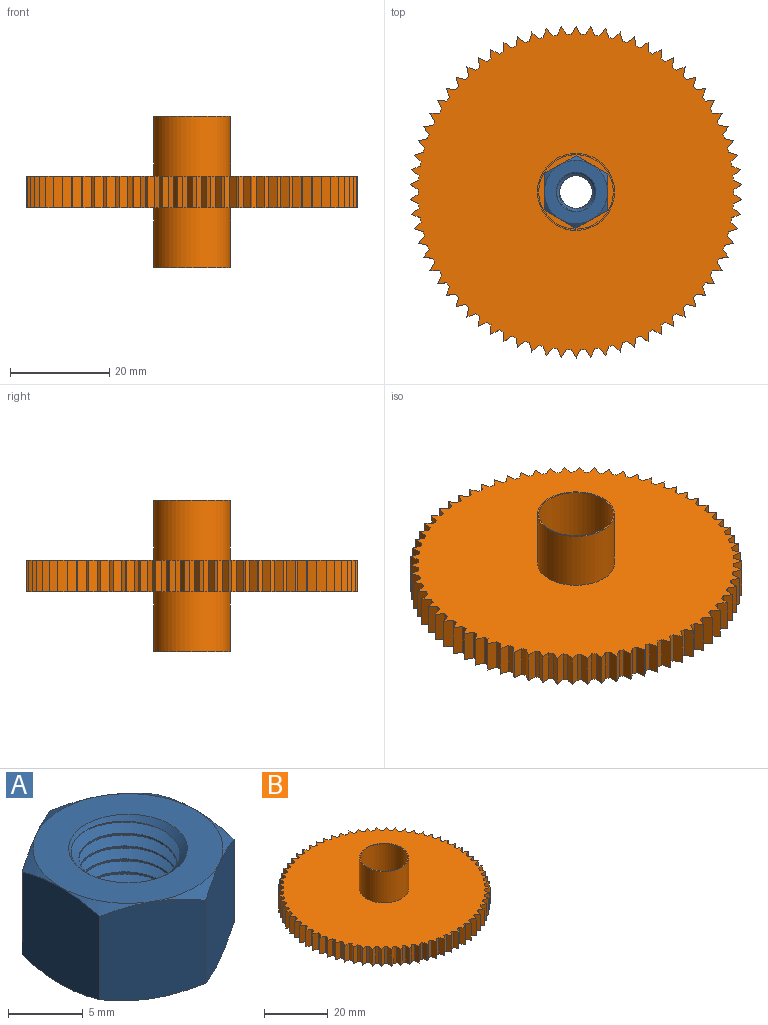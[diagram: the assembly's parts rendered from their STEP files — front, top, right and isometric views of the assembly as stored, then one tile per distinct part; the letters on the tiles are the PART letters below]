
ASSEMBLY  parts=2 mates=1
PART A: 26 faces, bbox 15.3x15.3x9.5 mm
  f0: plane 12.7x12.7mm, normal (0,0,1), area 77.2mm2, adj f7,f12,f13,f14,f15,f16,f17,f18
  f1: plane 8.55x6.95mm, normal (-0.5,0.87,0), area 55.3mm2, adj f2,f6,f13,f18,f21,f22
  f2: plane 8.55x7.94mm, normal (-1,0,0), area 55.3mm2, adj f1,f3,f17,f18,f22,f23
  f3: plane 8.55x6.95mm, normal (-0.5,-0.87,0), area 55.3mm2, adj f2,f4,f16,f17,f23,f24
  f4: plane 8.55x6.95mm, normal (0.5,-0.87,0), area 55.3mm2, adj f3,f5,f15,f16,f24,f25
  f5: plane 8.55x7.94mm, normal (1,0,0), area 55.3mm2, adj f4,f6,f14,f15,f20,f25
  f6: plane 8.55x6.95mm, normal (0.5,0.87,0), area 55.3mm2, adj f1,f5,f13,f14,f20,f21
  f7: cylinder r=3.97mm len=7.94mm, axis (0,0,-1), area 24.7mm2, adj f0,f8,f9,f11
  f8: plane 12.7x12.7mm, normal (0,0,-1), area 77.2mm2, adj f7,f19,f20,f21,f22,f23,f24,f25
  f9: bspline ~8.6x7.94mm, area 124.2mm2, adj f7,f10,f12,f19
  f10: cylinder r=3.28mm len=6.56mm, axis (0,0,1), area 16.9mm2, adj f9,f11,f12,f19
  f11: bspline ~8.33x7.94mm, area 124.1mm2, adj f7,f10,f12,f19
  f12: cone r=3.7mm half-angle=45deg, axis (0,0,1), area 11.3mm2, adj f0,f9,f10,f11
  f13: cone r=6.35mm half-angle=60deg, axis (0,0,-1), area 4mm2, adj f0,f1,f6
  f14: cone r=6.35mm half-angle=60deg, axis (0,0,-1), area 4mm2, adj f0,f5,f6
  f15: cone r=6.35mm half-angle=60deg, axis (0,0,-1), area 4mm2, adj f0,f4,f5
  f16: cone r=6.35mm half-angle=60deg, axis (0,0,-1), area 4mm2, adj f0,f3,f4
  f17: cone r=6.35mm half-angle=60deg, axis (0,0,-1), area 4mm2, adj f0,f2,f3
  f18: cone r=6.35mm half-angle=60deg, axis (0,0,-1), area 4mm2, adj f0,f1,f2
  f19: cone r=3.7mm half-angle=45deg, axis (0,0,-1), area 11.3mm2, adj f8,f9,f10,f11
  f20: cone r=6.35mm half-angle=60deg, axis (0,0,1), area 4mm2, adj f5,f6,f8
  f21: cone r=6.35mm half-angle=60deg, axis (0,0,1), area 4mm2, adj f1,f6,f8
  f22: cone r=6.35mm half-angle=60deg, axis (0,0,1), area 4mm2, adj f1,f2,f8
  f23: cone r=6.35mm half-angle=60deg, axis (0,0,1), area 4mm2, adj f2,f3,f8
  f24: cone r=6.35mm half-angle=60deg, axis (0,0,1), area 4mm2, adj f3,f4,f8
  f25: cone r=6.35mm half-angle=60deg, axis (0,0,1), area 4mm2, adj f4,f5,f8
PART B: 226 faces, bbox 66.7x66.8x30.5 mm
  f0: plane 14.99x14.99mm, normal (0,0,1), area 36.7mm2, adj f2,f3,f4,f5,f6,f7,f223
  f1: plane 14.99x14.99mm, normal (0,0,-1), area 36.7mm2, adj f2,f3,f4,f5,f6,f7,f8
  f2: plane 6.37x6.35mm, normal (-0.49,0.87,0), area 46.6mm2, adj f0,f1,f3,f7
  f3: plane 6.35x6.33mm, normal (0.51,0.86,0), area 46.6mm2, adj f0,f1,f2,f4
  f4: plane 7.33x6.35mm, normal (1,-0.01,0), area 46.6mm2, adj f0,f1,f3,f5
  f5: plane 6.37x6.35mm, normal (0.49,-0.87,0), area 46.6mm2, adj f0,f1,f4,f6
  f6: plane 6.35x6.33mm, normal (-0.51,-0.86,0), area 46.6mm2, adj f0,f1,f5,f7
  f7: plane 7.33x6.35mm, normal (-1,0.01,0), area 46.6mm2, adj f0,f1,f2,f6
  f8: cylinder r=7.49mm len=14.99mm, axis (0,0,-1), area 568mm2, adj f1,f9
  f9: plane 15.49x15.49mm, normal (0,0,-1), area 12.2mm2, adj f8,f10
  f10: cylinder r=7.75mm len=15.49mm, axis (0,0,-1), area 587.3mm2, adj f9,f222
  f11: plane 6.35x1.45mm, normal (0.76,0.65,0), area 12.1mm2, adj f12,f220,f221,f222
  f12: plane 6.35x1.79mm, normal (-0.94,0.34,0), area 12.1mm2, adj f11,f13,f220,f222
  f13: cylinder r=31.75mm len=6.35mm, axis (0,0,-1), area 6mm2, adj f12,f14,f220,f222
  f14: plane 6.35x1.36mm, normal (0.7,0.71,0), area 12.1mm2, adj f13,f15,f220,f222
  f15: plane 6.35x1.84mm, normal (-0.97,0.25,0), area 12.1mm2, adj f14,f16,f220,f222
  f16: cylinder r=31.75mm len=6.35mm, axis (0,0,-1), area 6mm2, adj f15,f17,f220,f222
  f17: plane 6.35x1.47mm, normal (0.64,0.77,0), area 12.1mm2, adj f16,f18,f220,f222
  f18: plane 6.35x1.88mm, normal (-0.99,0.16,0), area 12.1mm2, adj f17,f19,f220,f222
  f19: cylinder r=31.75mm len=6.35mm, axis (0,0,-1), area 6mm2, adj f18,f20,f220,f222
  f20: plane 6.35x1.57mm, normal (0.56,0.83,0), area 12.1mm2, adj f19,f21,f220,f222
  f21: plane 6.35x1.9mm, normal (-1,0.07,0), area 12.1mm2, adj f20,f22,f220,f222
  f22: cylinder r=31.75mm len=6.35mm, axis (0,0,-1), area 6mm2, adj f21,f23,f220,f222
  f23: plane 6.35x1.66mm, normal (0.49,0.87,0), area 12.1mm2, adj f22,f24,f220,f222
  f24: plane 6.35x1.9mm, normal (-1,-0.01,0), area 12.1mm2, adj f23,f25,f220,f222
  f25: cylinder r=31.75mm len=6.35mm, axis (0,0,-1), area 6mm2, adj f24,f26,f220,f222
  f26: plane 6.35x1.74mm, normal (0.41,0.91,0), area 12.1mm2, adj f25,f27,f220,f222
  f27: plane 6.35x1.89mm, normal (-0.99,-0.1,0), area 12.1mm2, adj f26,f28,f220,f222
  f28: cylinder r=31.75mm len=6.35mm, axis (0,0,-1), area 6mm2, adj f27,f29,f220,f222
  f29: plane 6.35x1.8mm, normal (0.32,0.95,0), area 12.1mm2, adj f28,f30,f220,f222
  f30: plane 6.35x1.87mm, normal (-0.98,-0.19,0), area 12.1mm2, adj f29,f31,f220,f222
  f31: cylinder r=31.75mm len=6.35mm, axis (0,0,-1), area 6mm2, adj f30,f32,f220,f222
  f32: plane 6.35x1.85mm, normal (0.24,0.97,0), area 12.1mm2, adj f31,f33,f220,f222
  f33: plane 6.35x1.83mm, normal (-0.96,-0.28,0), area 12.1mm2, adj f32,f34,f220,f222
  f34: cylinder r=31.75mm len=6.35mm, axis (0,0,-1), area 6mm2, adj f33,f35,f220,f222
  f35: plane 6.35x1.88mm, normal (0.15,0.99,0), area 12.1mm2, adj f34,f36,f220,f222
  f36: plane 6.35x1.77mm, normal (-0.93,-0.37,0), area 12.1mm2, adj f35,f37,f220,f222
  f37: cylinder r=31.75mm len=6.35mm, axis (0,0,-1), area 6mm2, adj f36,f38,f220,f222
  f38: plane 6.35x1.9mm, normal (0.06,1,0), area 12.1mm2, adj f37,f39,f220,f222
  f39: plane 6.35x1.7mm, normal (-0.89,-0.45,0), area 12.1mm2, adj f38,f40,f220,f222
  f40: cylinder r=31.75mm len=6.35mm, axis (0,0,-1), area 6mm2, adj f39,f41,f220,f222
  f41: plane 6.35x1.9mm, normal (-0.03,1,0), area 12.1mm2, adj f40,f42,f220,f222
  f42: plane 6.35x1.62mm, normal (-0.85,-0.53,0), area 12.1mm2, adj f41,f43,f220,f222
  f43: cylinder r=31.75mm len=6.35mm, axis (0,0,-1), area 6mm2, adj f42,f44,f220,f222
  f44: plane 6.35x1.89mm, normal (-0.12,0.99,0), area 12.1mm2, adj f43,f45,f220,f222
  f45: plane 6.35x1.52mm, normal (-0.8,-0.6,0), area 12.1mm2, adj f44,f46,f220,f222
  f46: cylinder r=31.75mm len=6.35mm, axis (0,0,-1), area 6mm2, adj f45,f47,f220,f222
  f47: plane 6.35x1.86mm, normal (-0.21,0.98,0), area 12.1mm2, adj f46,f48,f220,f222
  f48: plane 6.35x1.42mm, normal (-0.74,-0.67,0), area 12.1mm2, adj f47,f49,f220,f222
  f49: cylinder r=31.75mm len=6.35mm, axis (0,0,-1), area 6mm2, adj f48,f50,f220,f222
  f50: plane 6.35x1.82mm, normal (-0.29,0.96,0), area 12.1mm2, adj f49,f51,f220,f222
  f51: plane 6.35x1.4mm, normal (-0.68,-0.73,0), area 12.1mm2, adj f50,f52,f220,f222
  f52: cylinder r=31.75mm len=6.35mm, axis (0,0,-1), area 6mm2, adj f51,f53,f220,f222
  f53: plane 6.35x1.76mm, normal (-0.38,0.93,0), area 12.1mm2, adj f52,f54,f220,f222
  f54: plane 6.35x1.51mm, normal (-0.61,-0.79,0), area 12.1mm2, adj f53,f55,f220,f222
  f55: cylinder r=31.75mm len=6.35mm, axis (0,0,-1), area 6mm2, adj f54,f56,f220,f222
  f56: plane 6.35x1.69mm, normal (-0.46,0.89,0), area 12.1mm2, adj f55,f57,f220,f222
  f57: plane 6.35x1.61mm, normal (-0.54,-0.84,0), area 12.1mm2, adj f56,f58,f220,f222
  f58: cylinder r=31.75mm len=6.35mm, axis (0,0,-1), area 6mm2, adj f57,f59,f220,f222
  f59: plane 6.35x1.61mm, normal (-0.54,0.84,0), area 12.1mm2, adj f58,f60,f220,f222
  f60: plane 6.35x1.69mm, normal (-0.46,-0.89,0), area 12.1mm2, adj f59,f61,f220,f222
  f61: cylinder r=31.75mm len=6.35mm, axis (0,0,-1), area 6mm2, adj f60,f62,f220,f222
  f62: plane 6.35x1.51mm, normal (-0.61,0.79,0), area 12.1mm2, adj f61,f63,f220,f222
  f63: plane 6.35x1.76mm, normal (-0.38,-0.93,0), area 12.1mm2, adj f62,f64,f220,f222
  f64: cylinder r=31.75mm len=6.35mm, axis (0,0,-1), area 6mm2, adj f63,f65,f220,f222
  f65: plane 6.35x1.4mm, normal (-0.68,0.73,0), area 12.1mm2, adj f64,f66,f220,f222
  f66: plane 6.35x1.82mm, normal (-0.29,-0.96,0), area 12.1mm2, adj f65,f67,f220,f222
  f67: cylinder r=31.75mm len=6.35mm, axis (0,0,-1), area 6mm2, adj f66,f68,f220,f222
  f68: plane 6.35x1.42mm, normal (-0.74,0.67,0), area 12.1mm2, adj f67,f69,f220,f222
  f69: plane 6.35x1.86mm, normal (-0.21,-0.98,0), area 12.1mm2, adj f68,f70,f220,f222
  f70: cylinder r=31.75mm len=6.35mm, axis (0,0,-1), area 6mm2, adj f69,f71,f220,f222
  f71: plane 6.35x1.52mm, normal (-0.8,0.6,0), area 12.1mm2, adj f70,f72,f220,f222
  f72: plane 6.35x1.89mm, normal (-0.12,-0.99,0), area 12.1mm2, adj f71,f73,f220,f222
  f73: cylinder r=31.75mm len=6.35mm, axis (0,0,-1), area 6mm2, adj f72,f74,f220,f222
  f74: plane 6.35x1.62mm, normal (-0.85,0.53,0), area 12.1mm2, adj f73,f75,f220,f222
  f75: plane 6.35x1.9mm, normal (-0.03,-1,0), area 12.1mm2, adj f74,f76,f220,f222
  f76: cylinder r=31.75mm len=6.35mm, axis (0,0,-1), area 6mm2, adj f75,f77,f220,f222
  f77: plane 6.35x1.7mm, normal (-0.89,0.45,0), area 12.1mm2, adj f76,f78,f220,f222
  f78: plane 6.35x1.9mm, normal (0.06,-1,0), area 12.1mm2, adj f77,f79,f220,f222
  f79: cylinder r=31.75mm len=6.35mm, axis (0,0,-1), area 6mm2, adj f78,f80,f220,f222
  f80: plane 6.35x1.77mm, normal (-0.93,0.37,0), area 12.1mm2, adj f79,f81,f220,f222
  f81: plane 6.35x1.88mm, normal (0.15,-0.99,0), area 12.1mm2, adj f80,f82,f220,f222
  f82: cylinder r=31.75mm len=6.35mm, axis (0,0,-1), area 6mm2, adj f81,f83,f220,f222
  f83: plane 6.35x1.83mm, normal (-0.96,0.28,0), area 12.1mm2, adj f82,f84,f220,f222
  f84: plane 6.35x1.85mm, normal (0.24,-0.97,0), area 12.1mm2, adj f83,f85,f220,f222
  f85: cylinder r=31.75mm len=6.35mm, axis (0,0,-1), area 6mm2, adj f84,f86,f220,f222
  f86: plane 6.35x1.87mm, normal (-0.98,0.19,0), area 12.1mm2, adj f85,f87,f220,f222
  f87: plane 6.35x1.8mm, normal (0.32,-0.95,0), area 12.1mm2, adj f86,f88,f220,f222
  f88: cylinder r=31.75mm len=6.35mm, axis (0,0,-1), area 6mm2, adj f87,f89,f220,f222
  f89: plane 6.35x1.89mm, normal (-0.99,0.1,0), area 12.1mm2, adj f88,f90,f220,f222
  f90: plane 6.35x1.74mm, normal (0.41,-0.91,0), area 12.1mm2, adj f89,f91,f220,f222
  f91: cylinder r=31.75mm len=6.35mm, axis (0,0,-1), area 6mm2, adj f90,f92,f220,f222
  f92: plane 6.35x1.9mm, normal (-1,0.01,0), area 12.1mm2, adj f91,f93,f220,f222
  f93: plane 6.35x1.66mm, normal (0.49,-0.87,0), area 12.1mm2, adj f92,f94,f220,f222
  f94: cylinder r=31.75mm len=6.35mm, axis (0,0,-1), area 6mm2, adj f93,f95,f220,f222
  f95: plane 6.35x1.9mm, normal (-1,-0.07,0), area 12.1mm2, adj f94,f96,f220,f222
  f96: plane 6.35x1.57mm, normal (0.56,-0.83,0), area 12.1mm2, adj f95,f97,f220,f222
  f97: cylinder r=31.75mm len=6.35mm, axis (0,0,-1), area 6mm2, adj f96,f98,f220,f222
  f98: plane 6.35x1.88mm, normal (-0.99,-0.16,0), area 12.1mm2, adj f97,f99,f220,f222
  f99: plane 6.35x1.47mm, normal (0.64,-0.77,0), area 12.1mm2, adj f98,f100,f220,f222
  f100: cylinder r=31.75mm len=6.35mm, axis (0,0,-1), area 6mm2, adj f99,f101,f220,f222
  f101: plane 6.35x1.84mm, normal (-0.97,-0.25,0), area 12.1mm2, adj f100,f102,f220,f222
  f102: plane 6.35x1.36mm, normal (0.7,-0.71,0), area 12.1mm2, adj f101,f103,f220,f222
  f103: cylinder r=31.75mm len=6.35mm, axis (0,0,-1), area 6mm2, adj f102,f104,f220,f222
  f104: plane 6.35x1.79mm, normal (-0.94,-0.34,0), area 12.1mm2, adj f103,f105,f220,f222
  f105: plane 6.35x1.45mm, normal (0.76,-0.65,0), area 12.1mm2, adj f104,f106,f220,f222
  f106: cylinder r=31.75mm len=6.35mm, axis (0,0,-1), area 6mm2, adj f105,f107,f220,f222
  f107: plane 6.35x1.73mm, normal (-0.91,-0.42,0), area 12.1mm2, adj f106,f108,f220,f222
  f108: plane 6.35x1.56mm, normal (0.82,-0.58,0), area 12.1mm2, adj f107,f109,f220,f222
  f109: cylinder r=31.75mm len=6.35mm, axis (0,0,-1), area 6mm2, adj f108,f110,f220,f222
  f110: plane 6.35x1.65mm, normal (-0.87,-0.5,0), area 12.1mm2, adj f109,f111,f220,f222
  f111: plane 6.35x1.65mm, normal (0.87,-0.5,0), area 12.1mm2, adj f110,f112,f220,f222
  f112: cylinder r=31.75mm len=6.35mm, axis (0,0,-1), area 6mm2, adj f111,f113,f220,f222
  f113: plane 6.35x1.56mm, normal (-0.82,-0.58,0), area 12.1mm2, adj f112,f114,f220,f222
  f114: plane 6.35x1.73mm, normal (0.91,-0.42,0), area 12.1mm2, adj f113,f115,f220,f222
  f115: cylinder r=31.75mm len=6.35mm, axis (0,0,-1), area 6mm2, adj f114,f116,f220,f222
  f116: plane 6.35x1.45mm, normal (-0.76,-0.65,0), area 12.1mm2, adj f115,f117,f220,f222
  f117: plane 6.35x1.79mm, normal (0.94,-0.34,0), area 12.1mm2, adj f116,f118,f220,f222
  f118: cylinder r=31.75mm len=6.35mm, axis (0,0,-1), area 6mm2, adj f117,f119,f220,f222
  f119: plane 6.35x1.36mm, normal (-0.7,-0.71,0), area 12.1mm2, adj f118,f120,f220,f222
  f120: plane 6.35x1.84mm, normal (0.97,-0.25,0), area 12.1mm2, adj f119,f121,f220,f222
  f121: cylinder r=31.75mm len=6.35mm, axis (0,0,-1), area 6mm2, adj f120,f122,f220,f222
  f122: plane 6.35x1.47mm, normal (-0.64,-0.77,0), area 12.1mm2, adj f121,f123,f220,f222
  f123: plane 6.35x1.88mm, normal (0.99,-0.16,0), area 12.1mm2, adj f122,f124,f220,f222
  f124: cylinder r=31.75mm len=6.35mm, axis (0,0,-1), area 6mm2, adj f123,f125,f220,f222
  f125: plane 6.35x1.57mm, normal (-0.56,-0.83,0), area 12.1mm2, adj f124,f126,f220,f222
  f126: plane 6.35x1.9mm, normal (1,-0.07,0), area 12.1mm2, adj f125,f127,f220,f222
  f127: cylinder r=31.75mm len=6.35mm, axis (0,0,-1), area 6mm2, adj f126,f128,f220,f222
  f128: plane 6.35x1.66mm, normal (-0.49,-0.87,0), area 12.1mm2, adj f127,f129,f220,f222
  f129: plane 6.35x1.9mm, normal (1,0.01,0), area 12.1mm2, adj f128,f130,f220,f222
  f130: cylinder r=31.75mm len=6.35mm, axis (0,0,-1), area 6mm2, adj f129,f131,f220,f222
  f131: plane 6.35x1.74mm, normal (-0.41,-0.91,0), area 12.1mm2, adj f130,f132,f220,f222
  f132: plane 6.35x1.89mm, normal (0.99,0.1,0), area 12.1mm2, adj f131,f133,f220,f222
  f133: cylinder r=31.75mm len=6.35mm, axis (0,0,-1), area 6mm2, adj f132,f134,f220,f222
  f134: plane 6.35x1.8mm, normal (-0.32,-0.95,0), area 12.1mm2, adj f133,f135,f220,f222
  f135: plane 6.35x1.87mm, normal (0.98,0.19,0), area 12.1mm2, adj f134,f136,f220,f222
  f136: cylinder r=31.75mm len=6.35mm, axis (0,0,-1), area 6mm2, adj f135,f137,f220,f222
  f137: plane 6.35x1.85mm, normal (-0.24,-0.97,0), area 12.1mm2, adj f136,f138,f220,f222
  f138: plane 6.35x1.83mm, normal (0.96,0.28,0), area 12.1mm2, adj f137,f139,f220,f222
  f139: cylinder r=31.75mm len=6.35mm, axis (0,0,-1), area 6mm2, adj f138,f140,f220,f222
  f140: plane 6.35x1.88mm, normal (-0.15,-0.99,0), area 12.1mm2, adj f139,f141,f220,f222
  f141: plane 6.35x1.77mm, normal (0.93,0.37,0), area 12.1mm2, adj f140,f142,f220,f222
  f142: cylinder r=31.75mm len=6.35mm, axis (0,0,-1), area 6mm2, adj f141,f143,f220,f222
  f143: plane 6.35x1.9mm, normal (-0.06,-1,0), area 12.1mm2, adj f142,f144,f220,f222
  f144: plane 6.35x1.7mm, normal (0.89,0.45,0), area 12.1mm2, adj f143,f145,f220,f222
  f145: cylinder r=31.75mm len=6.35mm, axis (0,0,-1), area 6mm2, adj f144,f146,f220,f222
  f146: plane 6.35x1.9mm, normal (0.03,-1,0), area 12.1mm2, adj f145,f147,f220,f222
  f147: plane 6.35x1.62mm, normal (0.85,0.53,0), area 12.1mm2, adj f146,f148,f220,f222
  f148: cylinder r=31.75mm len=6.35mm, axis (0,0,-1), area 6mm2, adj f147,f149,f220,f222
  f149: plane 6.35x1.89mm, normal (0.12,-0.99,0), area 12.1mm2, adj f148,f150,f220,f222
  f150: plane 6.35x1.52mm, normal (0.8,0.6,0), area 12.1mm2, adj f149,f151,f220,f222
  f151: cylinder r=31.75mm len=6.35mm, axis (0,0,-1), area 6mm2, adj f150,f152,f220,f222
  f152: plane 6.35x1.86mm, normal (0.21,-0.98,0), area 12.1mm2, adj f151,f153,f220,f222
  f153: plane 6.35x1.42mm, normal (0.74,0.67,0), area 12.1mm2, adj f152,f154,f220,f222
  f154: cylinder r=31.75mm len=6.35mm, axis (0,0,-1), area 6mm2, adj f153,f155,f220,f222
  f155: plane 6.35x1.82mm, normal (0.29,-0.96,0), area 12.1mm2, adj f154,f156,f220,f222
  f156: plane 6.35x1.4mm, normal (0.68,0.73,0), area 12.1mm2, adj f155,f157,f220,f222
  f157: cylinder r=31.75mm len=6.35mm, axis (0,0,-1), area 6mm2, adj f156,f158,f220,f222
  f158: plane 6.35x1.76mm, normal (0.38,-0.93,0), area 12.1mm2, adj f157,f159,f220,f222
  f159: plane 6.35x1.51mm, normal (0.61,0.79,0), area 12.1mm2, adj f158,f160,f220,f222
  f160: cylinder r=31.75mm len=6.35mm, axis (0,0,-1), area 6mm2, adj f159,f161,f220,f222
  f161: plane 6.35x1.69mm, normal (0.46,-0.89,0), area 12.1mm2, adj f160,f162,f220,f222
  f162: plane 6.35x1.61mm, normal (0.54,0.84,0), area 12.1mm2, adj f161,f163,f220,f222
  f163: cylinder r=31.75mm len=6.35mm, axis (0,0,-1), area 6mm2, adj f162,f164,f220,f222
  f164: plane 6.35x1.61mm, normal (0.54,-0.84,0), area 12.1mm2, adj f163,f165,f220,f222
  f165: plane 6.35x1.69mm, normal (0.46,0.89,0), area 12.1mm2, adj f164,f166,f220,f222
  f166: cylinder r=31.75mm len=6.35mm, axis (0,0,-1), area 6mm2, adj f165,f167,f220,f222
  f167: plane 6.35x1.51mm, normal (0.61,-0.79,0), area 12.1mm2, adj f166,f168,f220,f222
  f168: plane 6.35x1.76mm, normal (0.38,0.93,0), area 12.1mm2, adj f167,f169,f220,f222
  f169: cylinder r=31.75mm len=6.35mm, axis (0,0,-1), area 6mm2, adj f168,f170,f220,f222
  f170: plane 6.35x1.4mm, normal (0.68,-0.73,0), area 12.1mm2, adj f169,f171,f220,f222
  f171: plane 6.35x1.82mm, normal (0.29,0.96,0), area 12.1mm2, adj f170,f172,f220,f222
  f172: cylinder r=31.75mm len=6.35mm, axis (0,0,-1), area 6mm2, adj f171,f173,f220,f222
  f173: plane 6.35x1.42mm, normal (0.74,-0.67,0), area 12.1mm2, adj f172,f174,f220,f222
  f174: plane 6.35x1.86mm, normal (0.21,0.98,0), area 12.1mm2, adj f173,f175,f220,f222
  f175: cylinder r=31.75mm len=6.35mm, axis (0,0,-1), area 6mm2, adj f174,f176,f220,f222
  f176: plane 6.35x1.52mm, normal (0.8,-0.6,0), area 12.1mm2, adj f175,f177,f220,f222
  f177: plane 6.35x1.89mm, normal (0.12,0.99,0), area 12.1mm2, adj f176,f178,f220,f222
  f178: cylinder r=31.75mm len=6.35mm, axis (0,0,-1), area 6mm2, adj f177,f179,f220,f222
  f179: plane 6.35x1.62mm, normal (0.85,-0.53,0), area 12.1mm2, adj f178,f180,f220,f222
  f180: plane 6.35x1.9mm, normal (0.03,1,0), area 12.1mm2, adj f179,f181,f220,f222
  f181: cylinder r=31.75mm len=6.35mm, axis (0,0,-1), area 6mm2, adj f180,f182,f220,f222
  f182: plane 6.35x1.7mm, normal (0.89,-0.45,0), area 12.1mm2, adj f181,f183,f220,f222
  f183: plane 6.35x1.9mm, normal (-0.06,1,0), area 12.1mm2, adj f182,f184,f220,f222
  f184: cylinder r=31.75mm len=6.35mm, axis (0,0,-1), area 6mm2, adj f183,f185,f220,f222
  f185: plane 6.35x1.77mm, normal (0.93,-0.37,0), area 12.1mm2, adj f184,f186,f220,f222
  f186: plane 6.35x1.88mm, normal (-0.15,0.99,0), area 12.1mm2, adj f185,f187,f220,f222
  f187: cylinder r=31.75mm len=6.35mm, axis (0,0,-1), area 6mm2, adj f186,f188,f220,f222
  f188: plane 6.35x1.83mm, normal (0.96,-0.28,0), area 12.1mm2, adj f187,f189,f220,f222
  f189: plane 6.35x1.85mm, normal (-0.24,0.97,0), area 12.1mm2, adj f188,f190,f220,f222
  f190: cylinder r=31.75mm len=6.35mm, axis (0,0,-1), area 6mm2, adj f189,f191,f220,f222
  f191: plane 6.35x1.87mm, normal (0.98,-0.19,0), area 12.1mm2, adj f190,f192,f220,f222
  f192: plane 6.35x1.8mm, normal (-0.32,0.95,0), area 12.1mm2, adj f191,f193,f220,f222
  f193: cylinder r=31.75mm len=6.35mm, axis (0,0,-1), area 6mm2, adj f192,f194,f220,f222
  f194: plane 6.35x1.89mm, normal (0.99,-0.1,0), area 12.1mm2, adj f193,f195,f220,f222
  f195: plane 6.35x1.74mm, normal (-0.41,0.91,0), area 12.1mm2, adj f194,f196,f220,f222
  f196: cylinder r=31.75mm len=6.35mm, axis (0,0,-1), area 6mm2, adj f195,f197,f220,f222
  f197: plane 6.35x1.9mm, normal (1,-0.01,0), area 12.1mm2, adj f196,f198,f220,f222
  f198: plane 6.35x1.66mm, normal (-0.49,0.87,0), area 12.1mm2, adj f197,f199,f220,f222
  f199: cylinder r=31.75mm len=6.35mm, axis (0,0,-1), area 6mm2, adj f198,f200,f220,f222
  f200: plane 6.35x1.9mm, normal (1,0.07,0), area 12.1mm2, adj f199,f201,f220,f222
  f201: plane 6.35x1.57mm, normal (-0.56,0.83,0), area 12.1mm2, adj f200,f202,f220,f222
  f202: cylinder r=31.75mm len=6.35mm, axis (0,0,-1), area 6mm2, adj f201,f203,f220,f222
  f203: plane 6.35x1.88mm, normal (0.99,0.16,0), area 12.1mm2, adj f202,f204,f220,f222
  f204: plane 6.35x1.47mm, normal (-0.64,0.77,0), area 12.1mm2, adj f203,f205,f220,f222
  f205: cylinder r=31.75mm len=6.35mm, axis (0,0,-1), area 6mm2, adj f204,f206,f220,f222
  f206: plane 6.35x1.84mm, normal (0.97,0.25,0), area 12.1mm2, adj f205,f207,f220,f222
  f207: plane 6.35x1.36mm, normal (-0.7,0.71,0), area 12.1mm2, adj f206,f208,f220,f222
  f208: cylinder r=31.75mm len=6.35mm, axis (0,0,-1), area 6mm2, adj f207,f209,f220,f222
  f209: plane 6.35x1.79mm, normal (0.94,0.34,0), area 12.1mm2, adj f208,f210,f220,f222
  f210: plane 6.35x1.45mm, normal (-0.76,0.65,0), area 12.1mm2, adj f209,f211,f220,f222
  f211: cylinder r=31.75mm len=6.35mm, axis (0,0,-1), area 6mm2, adj f210,f212,f220,f222
  f212: plane 6.35x1.73mm, normal (0.91,0.42,0), area 12.1mm2, adj f211,f213,f220,f222
  f213: plane 6.35x1.56mm, normal (-0.82,0.58,0), area 12.1mm2, adj f212,f214,f220,f222
  f214: cylinder r=31.75mm len=6.35mm, axis (0,0,-1), area 6mm2, adj f213,f215,f220,f222
  f215: plane 6.35x1.65mm, normal (0.87,0.5,0), area 12.1mm2, adj f214,f216,f220,f222
  f216: plane 6.35x1.65mm, normal (-0.87,0.5,0), area 12.1mm2, adj f215,f217,f220,f222
  f217: cylinder r=31.75mm len=6.35mm, axis (0,0,-1), area 6mm2, adj f216,f218,f220,f222
  f218: plane 6.35x1.56mm, normal (0.82,0.58,0), area 12.1mm2, adj f217,f219,f220,f222
  f219: plane 6.35x1.73mm, normal (-0.91,0.42,0), area 12.1mm2, adj f218,f220,f221,f222
  f220: plane 66.77x66.7mm, normal (0,0,1), area 3087.1mm2, adj f11,f12,f13,f14,f15,f16,f17,f18
  f221: cylinder r=31.75mm len=6.35mm, axis (0,0,-1), area 6mm2, adj f11,f219,f220,f222
  f222: plane 66.77x66.7mm, normal (0,0,-1), area 3087.1mm2, adj f10,f11,f12,f13,f14,f15,f16,f17
  f223: cylinder r=7.49mm len=14.99mm, axis (0,0,-1), area 568mm2, adj f0,f225
  f224: cylinder r=7.75mm len=15.49mm, axis (0,0,-1), area 587.3mm2, adj f220,f225
  f225: plane 15.49x15.49mm, normal (0,0,1), area 12.2mm2, adj f223,f224
PLACE A rot(axis=(0,0,-1),0.4deg) t=(0.09,0.01,-0.05)mm
PLACE B t=(0.09,0.01,-0.05)mm
MATE fastened A.f4 <-> B.f2  axis (0.49,-0.87,0) through (3.23,-5.51,-0.05)mm
